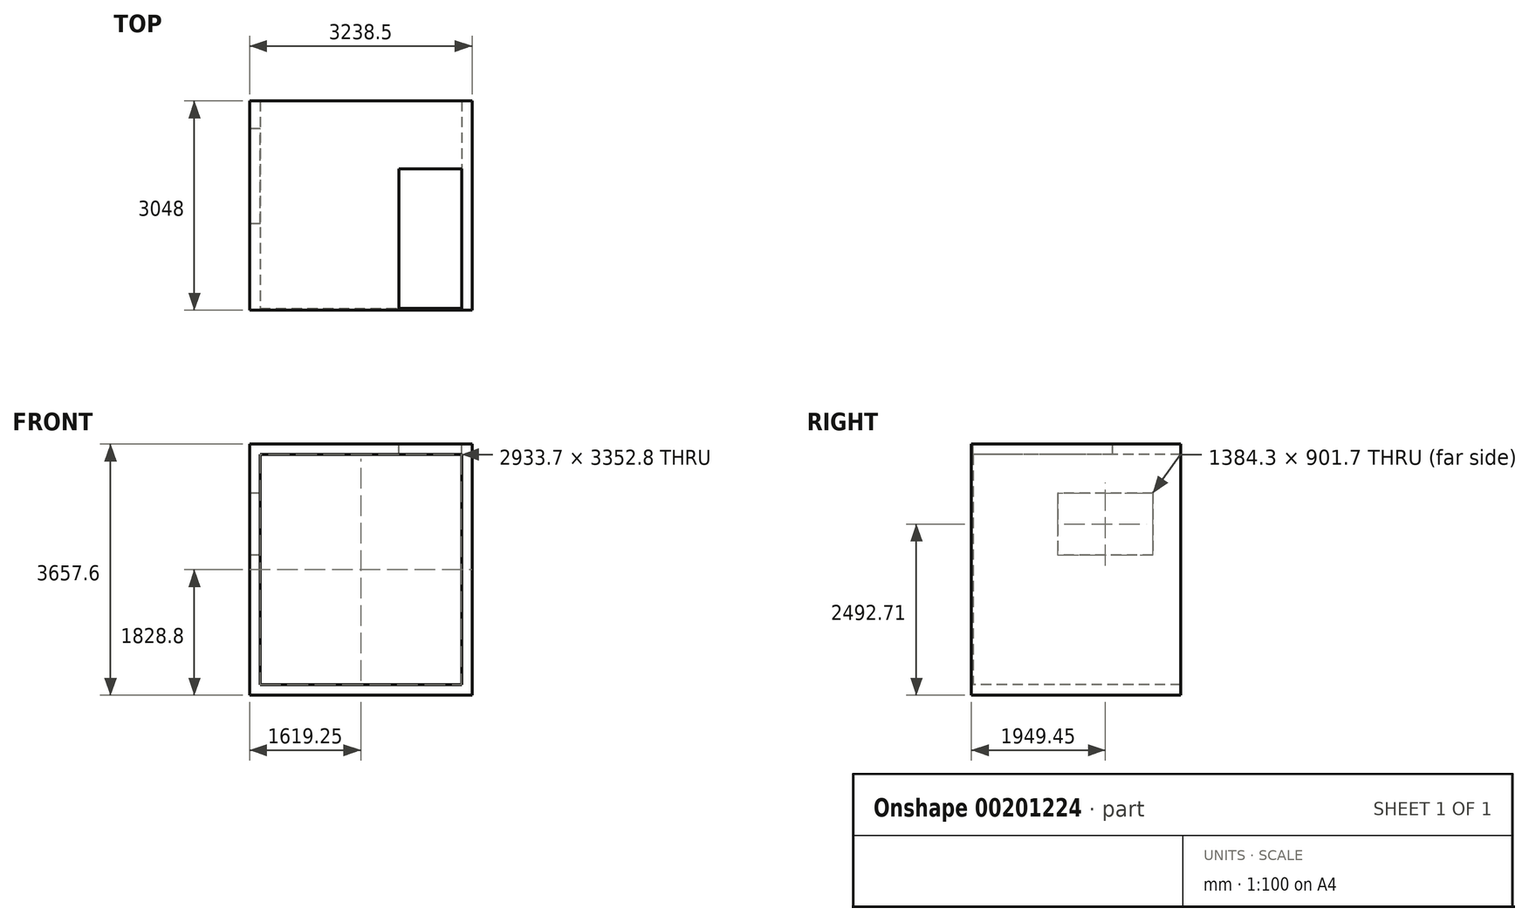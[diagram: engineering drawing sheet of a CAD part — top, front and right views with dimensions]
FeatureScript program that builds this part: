
annotation { "Feature Type Name" : "Feature", "Feature Type Description" : "" }
export const myFeature = defineFeature(function(context is Context, id is Id, definition is map)
    precondition{}
    {
        {
            var Q0;
            Q0=qCreatedBy(makeId("Front.planeOp"),FACE);
            var sketch = newSketch(context, id + "F0", { "sketchPlane" : qUnion([Q0])});
            skLineSegment(sketch, "E0.bottom", {"start": v(-1869.1, 2336.73) * mm, "end": v(1369.4, 2336.73) * mm});
            skLineSegment(sketch, "E0.top", {"start": v(-1869.1, -1320.87) * mm, "end": v(1369.4, -1320.87) * mm});
            skLineSegment(sketch, "E0.left", {"start": v(-1869.1, 2336.73) * mm, "end": v(-1869.1, -1320.87) * mm});
            skLineSegment(sketch, "E0.right", {"start": v(1369.4, 2336.73) * mm, "end": v(1369.4, -1320.87) * mm});
            skLineSegment(sketch, "E1.bottom", {"start": v(-1716.7, 2184.33) * mm, "end": v(1217, 2184.33) * mm});
            skLineSegment(sketch, "E1.top", {"start": v(-1716.7, -1168.47) * mm, "end": v(1217, -1168.47) * mm});
            skLineSegment(sketch, "E1.left", {"start": v(-1716.7, 2184.33) * mm, "end": v(-1716.7, -1168.47) * mm});
            skLineSegment(sketch, "E1.right", {"start": v(1217, 2184.33) * mm, "end": v(1217, -1168.47) * mm});
            skSolve(sketch);
        }
        {
            var Q0;
            Q0=makeQuery(id+"F0.imprint","IMPRINT",FACE,{"disambiguationData":[TD([[makeQuery(id+"F0.imprint","IMPRINT",EDGE,{"derivedFrom":sQuery(id+"F0.wireOp",EDGE,"E1.bottom")}),-1.0]])]});
            extrude(context, id + "F1", {"entities" : qUnion([Q0]), "oppositeDirection" : true, "depth" : 25.4 * mm});
        }
        {
            var Q0;
            Q0 = qSketchRegion(id + "F0", true);
            extrude(context, id + "F2", {"entities" : qUnion([Q0]), "oppositeDirection" : true, "depth" : 3048 * mm});
        }
        {
            var Q0;
            Q0=makeQuery(id+"F2.opExtrude","SWEPT_FACE",FACE,{"disambiguationData":[OSD([sQuery(id+"F0.wireOp",EDGE,"E0.bottom")])]});
            var sketch = newSketch(context, id + "F3", { "sketchPlane" : qUnion([Q0])});
            skLineSegment(sketch, "E2.bottom", {"start": v(1217, 2057.4) * mm, "end": v(302.6, 2057.4) * mm});
            skLineSegment(sketch, "E2.top", {"start": v(1217, 25.4) * mm, "end": v(302.6, 25.4) * mm});
            skLineSegment(sketch, "E2.left", {"start": v(1217, 2057.4) * mm, "end": v(1217, 25.4) * mm});
            skLineSegment(sketch, "E2.right", {"start": v(302.6, 2057.4) * mm, "end": v(302.6, 25.4) * mm});
            skSolve(sketch);
        }
        {
            var Q0;
            Q0=makeQuery(id+"F3.imprint","IMPRINT",FACE,{"disambiguationData":[TD([[makeQuery(id+"F3.imprint","IMPRINT",EDGE,{"derivedFrom":sQuery(id+"F3.wireOp",EDGE,"E2.bottom")}),1.0]])]});
            extrude(context, id + "F4", {"entities" : qUnion([Q0]), "operationType" : NewBodyOperationType.REMOVE, "endBound" : BoundingType.UP_TO_NEXT, "oppositeDirection" : true, "depth" : 25.4 * mm});
        }
        {
            var Q0;
            Q0=makeQuery(id+"F2.opExtrude","SWEPT_FACE",FACE,{"disambiguationData":[OSD([sQuery(id+"F0.wireOp",EDGE,"E0.left")])]});
            var sketch = newSketch(context, id + "F5", { "sketchPlane" : qUnion([Q0])});
            skLineSegment(sketch, "E3.bottom", {"start": v(-2641.6, 1622.69) * mm, "end": v(-1257.3, 1622.69) * mm});
            skLineSegment(sketch, "E3.top", {"start": v(-2641.6, 720.99) * mm, "end": v(-1257.3, 720.99) * mm});
            skLineSegment(sketch, "E3.left", {"start": v(-2641.6, 1622.69) * mm, "end": v(-2641.6, 720.99) * mm});
            skLineSegment(sketch, "E3.right", {"start": v(-1257.3, 1622.69) * mm, "end": v(-1257.3, 720.99) * mm});
            skSolve(sketch);
        }
        {
            var Q0;
            Q0=makeQuery(id+"F5.imprint","IMPRINT",FACE,{"disambiguationData":[TD([[makeQuery(id+"F5.imprint","IMPRINT",EDGE,{"derivedFrom":sQuery(id+"F5.wireOp",EDGE,"E3.bottom")}),-1.0]])]});
            extrude(context, id + "F6", {"entities" : qUnion([Q0]), "operationType" : NewBodyOperationType.REMOVE, "endBound" : BoundingType.UP_TO_NEXT, "oppositeDirection" : true, "depth" : 25.4 * mm});
        }
    });
